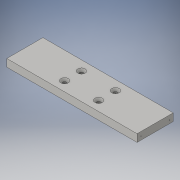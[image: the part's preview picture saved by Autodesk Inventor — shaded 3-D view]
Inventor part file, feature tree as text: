
AUTODESK INVENTOR PART (.ipt)
format: ipt  version: 2016 (Build 200138000, 138)  size: 121,344 bytes
history: native  units: in
note: dims shown in document units (in); Inventor stores cm internally (conversion verified against a paired STEP export)
features: sketch x3, hole x2, extrude x1
ambient origin geometry x8: Origin, YZ Plane, XZ Plane, XY Plane, X Axis, Y Axis, Z Axis, Center Point
bodies: Solid1 (feature_tree)
feature tree (6):
  extrude  "Extrusion1"  Depth=8.65in
  hole  "Hole1"  [1 undecoded]
  hole  "Hole2"  [1 undecoded]
  sketch  "Sketch1"  dims[d0=2.4in d1=8.65in]
  sketch  "Sketch2"  dims[d2=0.5in d3=0.0in d4=1.116in]
  sketch  "Sketch5"  dims[d5=0.0in d6=0.0in d7=0.642in d8=0.642in d9=2.258in d10=0.0in d11=0.0in d12=3.2in d13=3.192in d14=0.25in d15=0.75in d16=0.5in d17=0.25in d18=0.5635in d19=1.0in d20=0.8108in d21=1.9in d22=0.25in d23=0.3in d24=0.06in d25=0.75in d26=0.375in d27=0.25in d28=0.5635in d29=1.0in d30=0.8108in]
note: 2 required parameter values undecoded (feature->parameter linkage not recoverable at this tier; creation-order binding heuristic only, values carry confidence <= 0.55)
